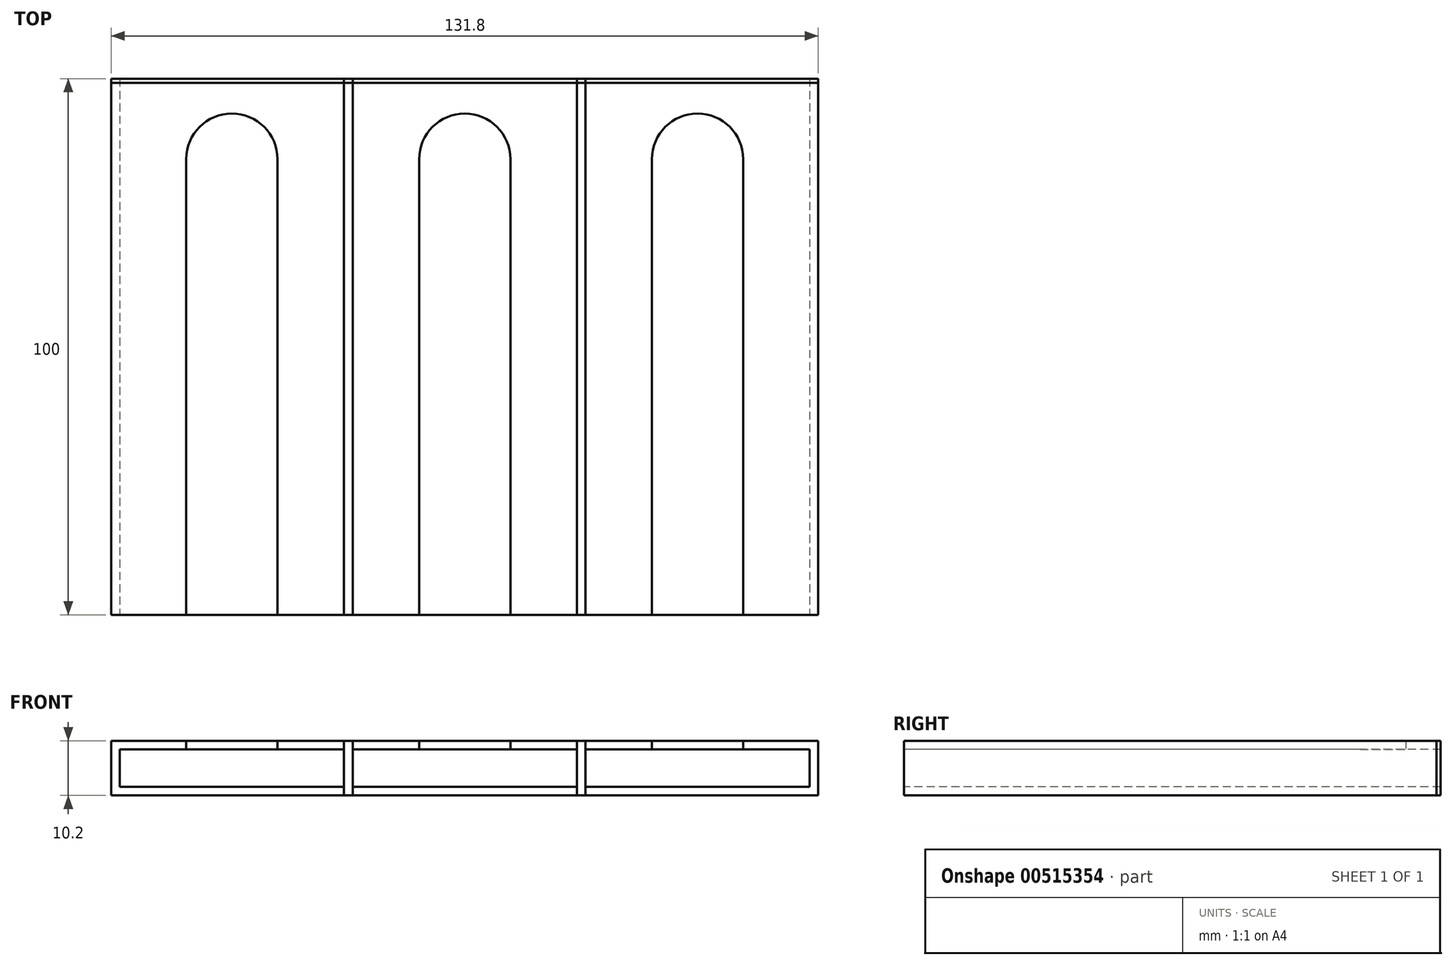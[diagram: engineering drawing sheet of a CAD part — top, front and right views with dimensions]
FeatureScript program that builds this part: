
annotation { "Feature Type Name" : "Feature", "Feature Type Description" : "" }
export const myFeature = defineFeature(function(context is Context, id is Id, definition is map)
    precondition{}
    {
        {
            var Q0;
            Q0=qCreatedBy(makeId("Top.planeOp"),FACE);
            var sketch = newSketch(context, id + "F0", { "sketchPlane" : qUnion([Q0])});
            skLineSegment(sketch, "E0.bottom", {"start": v(-56.34, 35.2) * mm, "end": v(-11.34, 35.2) * mm});
            skLineSegment(sketch, "E0.top", {"start": v(-56.34, -64.8) * mm, "end": v(-11.34, -64.8) * mm});
            skLineSegment(sketch, "E0.left", {"start": v(-56.34, 35.2) * mm, "end": v(-56.34, -64.8) * mm});
            skLineSegment(sketch, "E0.right", {"start": v(-11.34, 35.2) * mm, "end": v(-11.34, -64.8) * mm});
            skSolve(sketch);
        }
        {
            var Q0;
            Q0=makeQuery(id+"F0.imprint","IMPRINT",FACE,{"disambiguationData":[TD([[makeQuery(id+"F0.imprint","IMPRINT",EDGE,{"derivedFrom":sQuery(id+"F0.wireOp",EDGE,"E0.bottom")}),-1.0]])]});
            extrude(context, id + "F1", {"entities" : qUnion([Q0]), "depth" : 10.2 * mm});
        }
        {
            var Q0;
            Q0=makeQuery(id+"F1.opExtrude","CAP_FACE",FACE,{"disambiguationData":[OSD([sQuery(id+"F0.wireOp",EDGE,"E0.bottom"),sQuery(id+"F0.wireOp",EDGE,"E0.top"),sQuery(id+"F0.wireOp",EDGE,"E0.left"),sQuery(id+"F0.wireOp",EDGE,"E0.right")])],"isStart":false});
            var sketch = newSketch(context, id + "F2", { "sketchPlane" : qUnion([Q0])});
            skLineSegment(sketch, "E1.bottom", {"start": v(-42.34, -64.8) * mm, "end": v(-25.34, -64.8) * mm});
            skLineSegment(sketch, "E1.top", {"start": v(-42.34, 20.2) * mm, "end": v(-25.34, 20.2) * mm});
            skLineSegment(sketch, "E1.left", {"start": v(-42.34, -64.8) * mm, "end": v(-42.34, 20.2) * mm});
            skLineSegment(sketch, "E1.right", {"start": v(-25.34, -64.8) * mm, "end": v(-25.34, 20.2) * mm});
            skSolve(sketch);
        }
        {
            var Q0;
            Q0=qSketchRegion(id+"F2",true);
            extrude(context, id + "F3", {"entities" : qUnion([Q0]), "operationType" : NewBodyOperationType.REMOVE, "oppositeDirection" : true, "depth" : 8.6 * mm});
        }
        {
            var Q0;
            Q0=qCreatedBy(makeId("Top.planeOp"),FACE);
            var sketch = newSketch(context, id + "F4", { "sketchPlane" : qUnion([Q0])});
            skLineSegment(sketch, "E2.bottom", {"start": v(-56.34, 35.2) * mm, "end": v(-14.54, 35.2) * mm});
            skLineSegment(sketch, "E2.top", {"start": v(-56.34, -64.8) * mm, "end": v(-14.54, -64.8) * mm});
            skLineSegment(sketch, "E2.left", {"start": v(-56.34, 35.2) * mm, "end": v(-56.34, -64.8) * mm});
            skLineSegment(sketch, "E2.right", {"start": v(-14.54, 35.2) * mm, "end": v(-14.54, -64.8) * mm});
            skSolve(sketch);
        }
        {
            var Q0;
            Q0=makeQuery(id+"F4.imprint","IMPRINT",FACE,{"disambiguationData":[TD([[makeQuery(id+"F4.imprint","IMPRINT",EDGE,{"derivedFrom":sQuery(id+"F4.wireOp",EDGE,"E2.bottom")}),-1.0]])]});
            extrude(context, id + "F5", {"entities" : qUnion([Q0]), "depth" : 7 * mm});
        }
        {
            var Q0;
            Q0=makeQuery(id+"F5.opExtrude","SWEPT_BODY",BODY,{"disambiguationData":[OSD([sQuery(id+"F4.wireOp",EDGE,"E2.bottom"),sQuery(id+"F4.wireOp",EDGE,"E2.top"),sQuery(id+"F4.wireOp",EDGE,"E2.left"),sQuery(id+"F4.wireOp",EDGE,"E2.right")])]});
            transform(context, id + "F6", {"entities" : qUnion([Q0]), "transformType" : TransformType.TRANSLATION_3D, "dx" : 1.6 * mm, "dy" : 0 * mm, "dz" : 1.6 * mm, "makeCopy" : false});
        }
        {
            var Q0;
            Q0=makeQuery(id+"F5.opExtrude","SWEPT_BODY",BODY,{"disambiguationData":[OSD([sQuery(id+"F4.wireOp",EDGE,"E2.bottom"),sQuery(id+"F4.wireOp",EDGE,"E2.top"),sQuery(id+"F4.wireOp",EDGE,"E2.left"),sQuery(id+"F4.wireOp",EDGE,"E2.right")])]});
            var Q1;
            Q1=makeQuery(id+"F1.opExtrude","SWEPT_BODY",BODY,{"disambiguationData":[OSD([sQuery(id+"F0.wireOp",EDGE,"E0.bottom"),sQuery(id+"F0.wireOp",EDGE,"E0.top"),sQuery(id+"F0.wireOp",EDGE,"E0.left"),sQuery(id+"F0.wireOp",EDGE,"E0.right")])]});
            booleanBodies(context, id + "F7", {"operationType" : BooleanOperationType.SUBTRACTION, "tools" : qUnion([Q0]), "targets" : qUnion([Q1])});
        }
        {
            var Q0;
            Q0=qCreatedBy(makeId("Top.planeOp"),FACE);
            var sketch = newSketch(context, id + "F8", { "sketchPlane" : qUnion([Q0])});
            skCircle(sketch, "E3", {"center": v(-33.84, -64.8) * mm, "radius": 8.5 * mm});
            skSolve(sketch);
        }
        {
            var Q0;
            Q0=makeQuery(id+"F8.imprint","IMPRINT",FACE,{"disambiguationData":[TD([[makeQuery(id+"F8.imprint","IMPRINT",EDGE,{"derivedFrom":sQuery(id+"F8.wireOp",EDGE,"E3")}),1.0]])]});
            extrude(context, id + "F9", {"entities" : qUnion([Q0]), "depth" : 10 * mm});
        }
        {
            var Q0;
            Q0=makeQuery(id+"F9.opExtrude","SWEPT_BODY",BODY,{"disambiguationData":[OSD([sQuery(id+"F8.wireOp",EDGE,"E3")])]});
            transform(context, id + "F10", {"entities" : qUnion([Q0]), "transformType" : TransformType.TRANSLATION_3D, "dx" : 0 * mm, "dy" : 85 * mm, "dz" : 4 * mm, "makeCopy" : false});
        }
        {
            var Q0;
            Q0=makeQuery(id+"F9.opExtrude","SWEPT_BODY",BODY,{"disambiguationData":[OSD([sQuery(id+"F8.wireOp",EDGE,"E3")])]});
            var Q1;
            Q1=makeQuery(id+"F1.opExtrude","SWEPT_BODY",BODY,{"disambiguationData":[OSD([sQuery(id+"F0.wireOp",EDGE,"E0.bottom"),sQuery(id+"F0.wireOp",EDGE,"E0.top"),sQuery(id+"F0.wireOp",EDGE,"E0.left"),sQuery(id+"F0.wireOp",EDGE,"E0.right")])]});
            booleanBodies(context, id + "F11", {"operationType" : BooleanOperationType.SUBTRACTION, "tools" : qUnion([Q0]), "targets" : qUnion([Q1])});
        }
        {
            var Q0;
            Q0=makeQuery(id+"F1.opExtrude","SWEPT_BODY",BODY,{"disambiguationData":[OSD([sQuery(id+"F0.wireOp",EDGE,"E0.bottom"),sQuery(id+"F0.wireOp",EDGE,"E0.top"),sQuery(id+"F0.wireOp",EDGE,"E0.left"),sQuery(id+"F0.wireOp",EDGE,"E0.right")])]});
            transform(context, id + "F12", {"entities" : qUnion([Q0]), "transformType" : TransformType.TRANSLATION_3D, "dx" : 43.4 * mm, "dy" : 0 * mm, "dz" : 0 * mm, "makeCopy" : true});
        }
        {
            var Q0;
            Q0=makeQuery(id+"F12.opPattern","COPY",BODY,{"derivedFrom":makeQuery(id+"F1.opExtrude","SWEPT_BODY",BODY,{"disambiguationData":[OSD([sQuery(id+"F0.wireOp",EDGE,"E0.bottom"),sQuery(id+"F0.wireOp",EDGE,"E0.top"),sQuery(id+"F0.wireOp",EDGE,"E0.left"),sQuery(id+"F0.wireOp",EDGE,"E0.right")])]}),"instanceName":"1"});
            transform(context, id + "F13", {"entities" : qUnion([Q0]), "transformType" : TransformType.TRANSLATION_3D, "dx" : 43.4 * mm, "dy" : 0 * mm, "dz" : 0 * mm, "makeCopy" : true});
        }
        {
            var Q0;
            Q0=makeQuery(id+"F12.opPattern","COPY",FACE,{"derivedFrom":makeQuery(id+"F1.opExtrude","SWEPT_FACE",FACE,{"disambiguationData":[OSD([sQuery(id+"F0.wireOp",EDGE,"E0.bottom")])]}),"instanceName":"1"});
            var sketch = newSketch(context, id + "F14", { "sketchPlane" : qUnion([Q0])});
            skLineSegment(sketch, "E4.bottom", {"start": v(-75.46, 10.2) * mm, "end": v(56.34, 10.2) * mm});
            skLineSegment(sketch, "E4.top", {"start": v(-75.46, 0) * mm, "end": v(56.34, 0) * mm});
            skLineSegment(sketch, "E4.left", {"start": v(-75.46, 10.2) * mm, "end": v(-75.46, 0) * mm});
            skLineSegment(sketch, "E4.right", {"start": v(56.34, 10.2) * mm, "end": v(56.34, 0) * mm});
            skSolve(sketch);
        }
        {
            var Q0;
            Q0=qSketchRegion(id+"F14",true);
            extrude(context, id + "F15", {"entities" : qUnion([Q0]), "oppositeDirection" : true, "depth" : 0.8 * mm});
        }
    });
